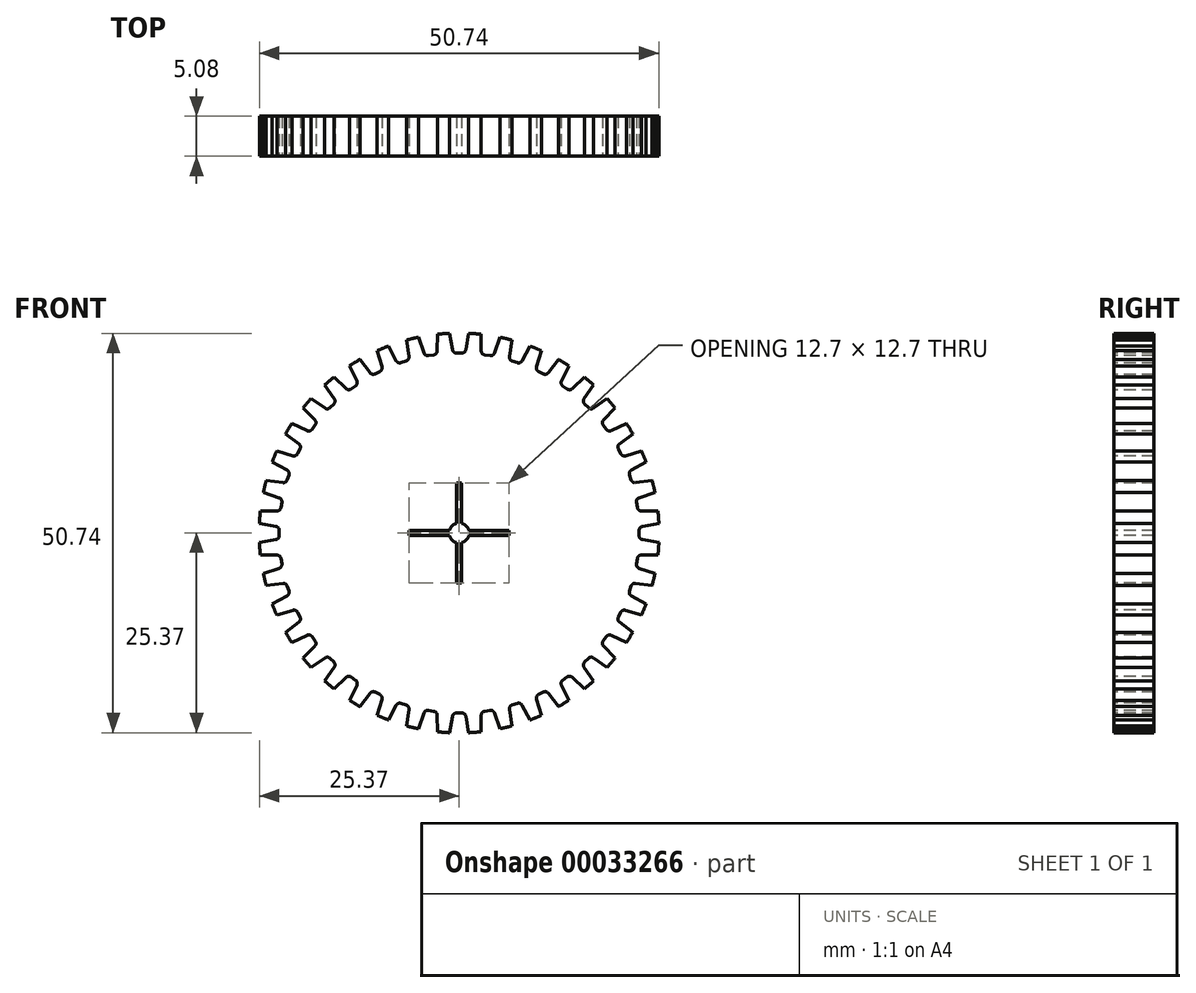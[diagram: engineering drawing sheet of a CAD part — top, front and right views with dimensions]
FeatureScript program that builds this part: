
annotation { "Feature Type Name" : "Feature", "Feature Type Description" : "" }
export const myFeature = defineFeature(function(context is Context, id is Id, definition is map)
    precondition{}
    {
        {
            var Q0;
            Q0=qCreatedBy(makeId("Front.planeOp"),FACE);
            var sketch = newSketch(context, id + "F0", { "sketchPlane" : qUnion([Q0])});
            skCircle(sketch, "E0", {"center": v(0, 0) * mm, "radius": 25.4 * mm});
            skSolve(sketch);
        }
        {
            var Q0;
            Q0 = qSketchRegion(id + "F0", true);
            extrude(context, id + "F1", {"entities" : qUnion([Q0]), "depth" : 5.08 * mm});
        }
        {
            var Q0;
            Q0=makeQuery(id+"F1.opExtrude","CAP_FACE",FACE,{"disambiguationData":[OSD([sQuery(id+"F0.wireOp",EDGE,"E0")])],"isStart":false});
            var sketch = newSketch(context, id + "F2", { "sketchPlane" : qUnion([Q0])});
            skLineSegment(sketch, "E1", {"start": v(0, 22.86) * mm, "end": v(0.34, 22.86) * mm});
            skLineSegment(sketch, "E2", {"start": v(0.84, 23.28) * mm, "end": v(1.21, 25.37) * mm});
            skPoint(sketch, "E3.visualSharp", {"position": v(0.77, 22.86) * mm});
            skArc(sketch, "E3.filletArc", {"start": v(0.34, 22.86) * mm, "mid": v(0.67, 22.98) * mm, "end": v(0.84, 23.28) * mm});
            skLineSegment(sketch, "E4.MirrorCS", {"start": v(0, 22.86) * mm, "end": v(-0.34, 22.86) * mm});
            skArc(sketch, "E5.MirrorCS", {"start": v(-0.34, 22.86) * mm, "mid": v(-0.67, 22.98) * mm, "end": v(-0.84, 23.28) * mm});
            skPoint(sketch, "E6.MirrorP", {"position": v(-0.77, 22.86) * mm});
            skLineSegment(sketch, "E7.MirrorCS", {"start": v(-0.84, 23.28) * mm, "end": v(-1.21, 25.37) * mm});
            skLineSegment(sketch, "E8", {"start": v(-1.21, 25.37) * mm, "end": v(-1.21, 25.98) * mm});
            skLineSegment(sketch, "E9", {"start": v(-1.21, 25.98) * mm, "end": v(1.21, 25.98) * mm});
            skLineSegment(sketch, "E10", {"start": v(1.21, 25.98) * mm, "end": v(1.21, 25.37) * mm});
            skSolve(sketch);
        }
        {
            var Q0;
            {var subQ0=sQuery(id+"F2.wireOp",EDGE,"E8");Q0=makeQuery(id+"F2.imprint","IMPRINT",FACE,{"disambiguationData":[TD([[makeQuery(id+"F2.imprint","IMPRINT",EDGE,{"derivedFrom":subQ0}),-1.0]])]});}
            var Q1;
            Q1=makeQuery(id+"F2.imprint","IMPRINT",FACE,{"disambiguationData":[TD([[makeQuery(id+"F2.imprint","IMPRINT",EDGE,{"derivedFrom":sQuery(id+"F2.wireOp",EDGE,"E1")}),1.0]])]});
            extrude(context, id + "F3", {"entities" : qUnion([Q0, Q1]), "operationType" : NewBodyOperationType.REMOVE, "endBound" : BoundingType.THROUGH_ALL, "oppositeDirection" : true, "depth" : 25.4 * mm});
        }
        {
            var Q0;
            Q0=makeQuery(id+"F3.boolean.opBoolean","COPY",FACE,{"derivedFrom":makeQuery(id+"F3.opExtrude","SWEPT_FACE",FACE,{"disambiguationData":[OSD([sQuery(id+"F2.wireOp",EDGE,"E7.MirrorCS")])]})});
            var Q1;
            Q1=makeQuery(id+"F3.boolean.opBoolean","COPY",FACE,{"derivedFrom":makeQuery(id+"F3.opExtrude","SWEPT_FACE",FACE,{"disambiguationData":[OSD([sQuery(id+"F2.wireOp",EDGE,"E5.MirrorCS")])]})});
            var Q2;
            Q2=makeQuery(id+"F3.boolean.opBoolean","COPY",FACE,{"derivedFrom":makeQuery(id+"F3.opExtrude","SWEPT_FACE",FACE,{"disambiguationData":[OSD([sQuery(id+"F2.wireOp",EDGE,"E1"),sQuery(id+"F2.wireOp",EDGE,"E4.MirrorCS")])]})});
            var Q3;
            Q3=makeQuery(id+"F3.boolean.opBoolean","COPY",FACE,{"derivedFrom":makeQuery(id+"F3.opExtrude","SWEPT_FACE",FACE,{"disambiguationData":[OSD([sQuery(id+"F2.wireOp",EDGE,"E2")])]})});
            var Q4;
            Q4=makeQuery(id+"F3.boolean.opBoolean","COPY",FACE,{"derivedFrom":makeQuery(id+"F3.opExtrude","SWEPT_FACE",FACE,{"disambiguationData":[OSD([sQuery(id+"F2.wireOp",EDGE,"E3.filletArc")])]})});
            var Q5;
            Q5=makeQuery(id+"F1.opExtrude","SWEPT_FACE",FACE,{"disambiguationData":[OSD([sQuery(id+"F0.wireOp",EDGE,"E0")])]});
            circularPattern(context, id + "F4", {"patternType" : PatternType.FACE, "faces" : qUnion([Q0, Q1, Q2, Q3, Q4]), "axis" : qUnion([Q5]), "angle" : 360 * degree, "instanceCount" : 40, "equalSpace" : true});
        }
        {
            var Q0;
            Q0=makeQuery(id+"F1.opExtrude","CAP_FACE",FACE,{"disambiguationData":[OSD([sQuery(id+"F0.wireOp",EDGE,"E0")])],"isStart":false});
            var sketch = newSketch(context, id + "F5", { "sketchPlane" : qUnion([Q0])});
            skLineSegment(sketch, "E11.bottom", {"start": v(-6.35, 0.32) * mm, "end": v(-1.23, 0.32) * mm});
            skLineSegment(sketch, "E11.top", {"start": v(-6.35, -0.32) * mm, "end": v(-1.23, -0.32) * mm});
            skLineSegment(sketch, "E11.left", {"start": v(-6.35, 0.32) * mm, "end": v(-6.35, -0.32) * mm});
            skLineSegment(sketch, "E11.right", {"start": v(6.35, 0.32) * mm, "end": v(6.35, -0.32) * mm});
            skLineSegment(sketch, "E12.bottom", {"start": v(-0.32, 6.35) * mm, "end": v(0.32, 6.35) * mm});
            skLineSegment(sketch, "E12.top", {"start": v(-0.32, -6.35) * mm, "end": v(0.32, -6.35) * mm});
            skLineSegment(sketch, "E12.left", {"start": v(-0.32, 6.35) * mm, "end": v(-0.32, 1.23) * mm});
            skLineSegment(sketch, "E12.right", {"start": v(0.32, 6.35) * mm, "end": v(0.32, 1.23) * mm});
            skArc(sketch, "E13", {"start": v(-1.23, -0.32) * mm, "mid": v(-0.9, -0.9) * mm, "end": v(-0.32, -1.23) * mm});
            skLineSegment(sketch, "E14.trimOffspring", {"start": v(1.23, 0.32) * mm, "end": v(6.35, 0.32) * mm});
            skLineSegment(sketch, "E15.trimOffspring", {"start": v(-0.32, -1.23) * mm, "end": v(-0.32, -6.35) * mm});
            skArc(sketch, "E16.trimOffspring", {"start": v(0.32, -1.23) * mm, "mid": v(0.9, -0.9) * mm, "end": v(1.23, -0.32) * mm});
            skLineSegment(sketch, "E17.trimOffspring", {"start": v(1.23, -0.32) * mm, "end": v(6.35, -0.32) * mm});
            skLineSegment(sketch, "E18.trimOffspring", {"start": v(0.32, -1.23) * mm, "end": v(0.32, -6.35) * mm});
            skArc(sketch, "E19.trimOffspring", {"start": v(1.23, 0.32) * mm, "mid": v(0.9, 0.9) * mm, "end": v(0.32, 1.23) * mm});
            skArc(sketch, "E20.trimOffspring", {"start": v(-0.32, 1.23) * mm, "mid": v(-0.9, 0.9) * mm, "end": v(-1.23, 0.32) * mm});
            skSolve(sketch);
        }
        {
            var Q0;
            Q0=makeQuery(id+"F5.imprint","IMPRINT",FACE,{"disambiguationData":[TD([[makeQuery(id+"F5.imprint","IMPRINT",EDGE,{"derivedFrom":sQuery(id+"F5.wireOp",EDGE,"E11.bottom")}),-1.0]])]});
            extrude(context, id + "F6", {"entities" : qUnion([Q0]), "operationType" : NewBodyOperationType.REMOVE, "endBound" : BoundingType.THROUGH_ALL, "oppositeDirection" : true, "depth" : 25.4 * mm});
        }
    });
